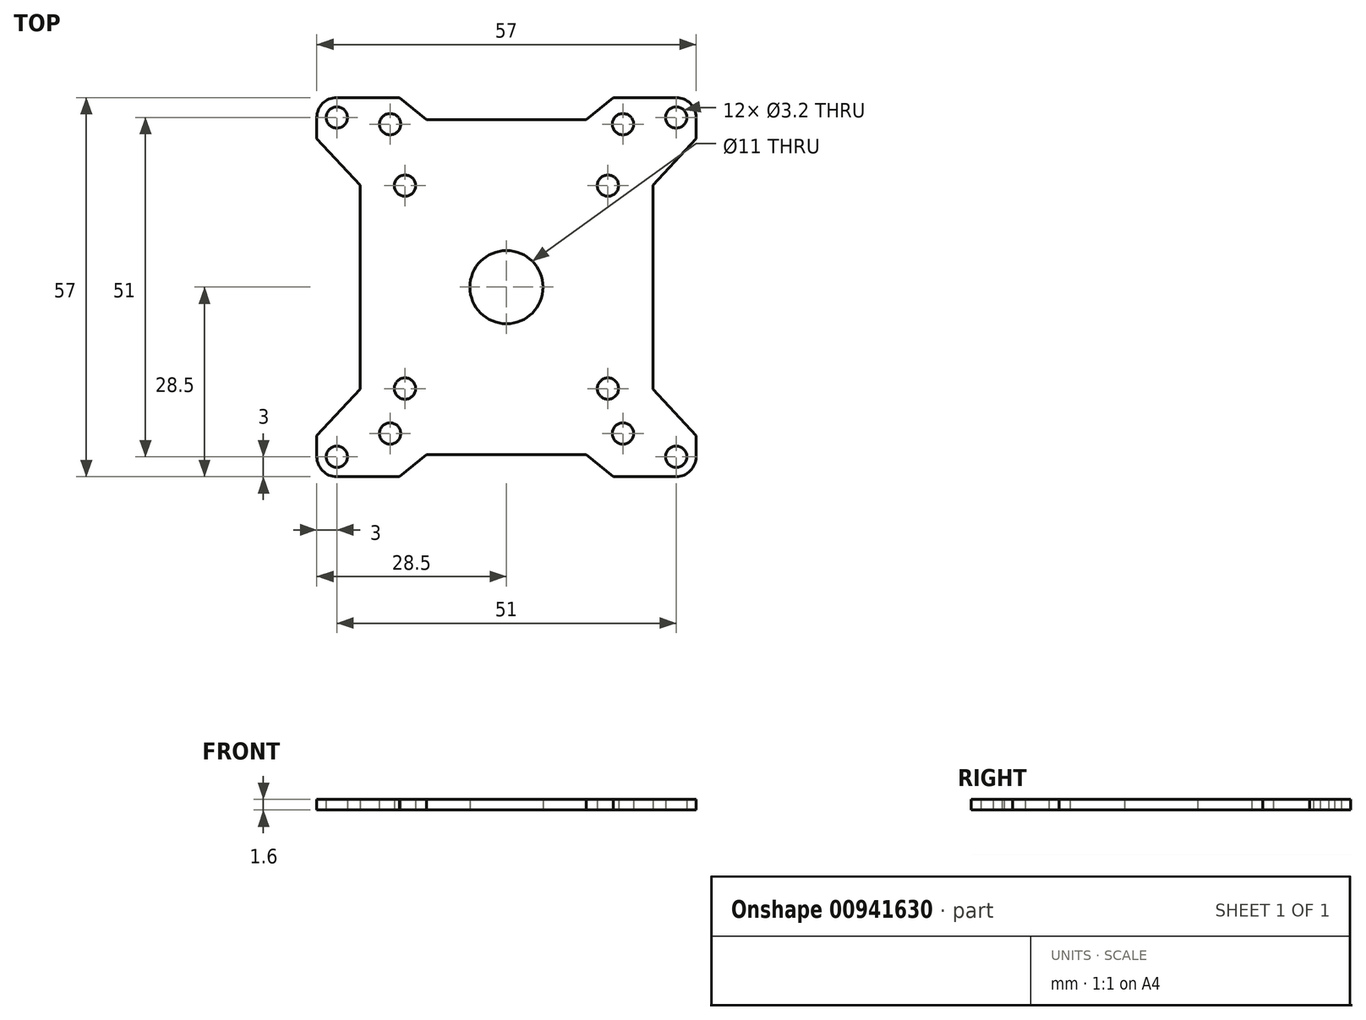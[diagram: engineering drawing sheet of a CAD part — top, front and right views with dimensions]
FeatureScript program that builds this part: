
annotation { "Feature Type Name" : "Feature", "Feature Type Description" : "" }
export const myFeature = defineFeature(function(context is Context, id is Id, definition is map)
    precondition{}
    {
        {
            var Q0;
            Q0=qCreatedBy(makeId("Top.planeOp"),FACE);
            var sketch = newSketch(context, id + "F0", { "sketchPlane" : qUnion([Q0])});
            skCircle(sketch, "E0.0", {"center": v(-17.5, -30) * mm, "radius": 1.6 * mm});
            skCircle(sketch, "E0.1", {"center": v(-17.5, 16.5) * mm, "radius": 1.6 * mm});
            skCircle(sketch, "E0.2", {"center": v(17.5, 16.5) * mm, "radius": 1.6 * mm});
            skCircle(sketch, "E0.3", {"center": v(17.5, -30) * mm, "radius": 1.6 * mm});
            skCircle(sketch, "E0.4", {"center": v(-15.25, 7.25) * mm, "radius": 1.6 * mm});
            skCircle(sketch, "E0.5", {"center": v(-15.25, -23.25) * mm, "radius": 1.6 * mm});
            skCircle(sketch, "E0.6", {"center": v(15.25, 7.25) * mm, "radius": 1.6 * mm});
            skCircle(sketch, "E0.7", {"center": v(15.25, -23.25) * mm, "radius": 1.6 * mm});
            skLineSegment(sketch, "E1", {"start": v(-15.25, 7.25) * mm, "end": v(15.25, -23.25) * mm, "construction": true});
            skLineSegment(sketch, "E2", {"start": v(-15.25, -23.25) * mm, "end": v(15.25, 7.25) * mm, "construction": true});
            skPoint(sketch, "E3", {"position": v(0, -8) * mm});
            skCircle(sketch, "E4.0", {"center": v(25.5, -33.5) * mm, "radius": 1.6 * mm});
            skCircle(sketch, "E4.1", {"center": v(-25.5, -33.5) * mm, "radius": 1.6 * mm});
            skCircle(sketch, "E4.2", {"center": v(-25.5, 17.5) * mm, "radius": 1.6 * mm});
            skPoint(sketch, "E5.visualSharp", {"position": v(-28.5, 20.5) * mm});
            skArc(sketch, "E5.filletArc", {"start": v(-25.5, 20.5) * mm, "mid": v(-27.62, 19.62) * mm, "end": v(-28.5, 17.5) * mm});
            skLineSegment(sketch, "E6", {"start": v(-25.5, 20.5) * mm, "end": v(-16.05, 20.5) * mm});
            skLineSegment(sketch, "E7", {"start": v(-16.05, 20.5) * mm, "end": v(-12, 17.2) * mm});
            skLineSegment(sketch, "E8", {"start": v(-12, 17.2) * mm, "end": v(0, 17.2) * mm});
            skLineSegment(sketch, "E9", {"start": v(-28.5, 17.5) * mm, "end": v(-28.5, 14.32) * mm});
            skLineSegment(sketch, "E10", {"start": v(-28.5, 14.32) * mm, "end": v(-22, 7.31) * mm});
            skLineSegment(sketch, "E11", {"start": v(-22, 7.31) * mm, "end": v(-22, -8) * mm});
            skLineSegment(sketch, "E12", {"start": v(0, -8) * mm, "end": v(-36.69, -8) * mm, "construction": true});
            skLineSegment(sketch, "E13.MirrorCS", {"start": v(-22, -23.31) * mm, "end": v(-22, -8) * mm});
            skLineSegment(sketch, "E14.MirrorCS", {"start": v(-28.5, -30.32) * mm, "end": v(-22, -23.31) * mm});
            skLineSegment(sketch, "E15.MirrorCS", {"start": v(-28.5, -33.5) * mm, "end": v(-28.5, -30.32) * mm});
            skArc(sketch, "E16.MirrorCS", {"start": v(-25.5, -36.5) * mm, "mid": v(-27.62, -35.62) * mm, "end": v(-28.5, -33.5) * mm});
            skLineSegment(sketch, "E17.MirrorCS", {"start": v(-25.5, -36.5) * mm, "end": v(-16.05, -36.5) * mm});
            skLineSegment(sketch, "E18.MirrorCS", {"start": v(-16.05, -36.5) * mm, "end": v(-12, -33.2) * mm});
            skLineSegment(sketch, "E19.MirrorCS", {"start": v(-12, -33.2) * mm, "end": v(0, -33.2) * mm});
            skLineSegment(sketch, "E20.MirrorCS", {"start": v(16.05, -36.5) * mm, "end": v(12, -33.2) * mm});
            skLineSegment(sketch, "E21.MirrorCS", {"start": v(25.5, -36.5) * mm, "end": v(16.05, -36.5) * mm});
            skArc(sketch, "E22.MirrorCS", {"start": v(25.5, -36.5) * mm, "mid": v(27.62, -35.62) * mm, "end": v(28.5, -33.5) * mm});
            skLineSegment(sketch, "E23.MirrorCS", {"start": v(28.5, -33.5) * mm, "end": v(28.5, -30.32) * mm});
            skLineSegment(sketch, "E24.MirrorCS", {"start": v(28.5, -30.32) * mm, "end": v(22, -23.31) * mm});
            skLineSegment(sketch, "E25.MirrorCS", {"start": v(22, -23.31) * mm, "end": v(22, -8) * mm});
            skLineSegment(sketch, "E26.MirrorCS", {"start": v(22, 7.31) * mm, "end": v(22, -8) * mm});
            skLineSegment(sketch, "E27.MirrorCS", {"start": v(28.5, 14.32) * mm, "end": v(22, 7.31) * mm});
            skLineSegment(sketch, "E28.MirrorCS", {"start": v(28.5, 17.5) * mm, "end": v(28.5, 14.32) * mm});
            skArc(sketch, "E29.MirrorCS", {"start": v(25.5, 20.5) * mm, "mid": v(27.62, 19.62) * mm, "end": v(28.5, 17.5) * mm});
            skLineSegment(sketch, "E30.MirrorCS", {"start": v(25.5, 20.5) * mm, "end": v(16.05, 20.5) * mm});
            skLineSegment(sketch, "E31.MirrorCS", {"start": v(16.05, 20.5) * mm, "end": v(12, 17.2) * mm});
            skLineSegment(sketch, "E32.MirrorCS", {"start": v(12, -33.2) * mm, "end": v(0, -33.2) * mm});
            skLineSegment(sketch, "E33.MirrorCS", {"start": v(12, 17.2) * mm, "end": v(0, 17.2) * mm});
            skCircle(sketch, "E34.0", {"center": v(0, -8) * mm, "radius": 5.5 * mm});
            skCircle(sketch, "E35.0", {"center": v(25.5, 17.5) * mm, "radius": 1.6 * mm});
            skSolve(sketch);
        }
        {
            var Q0;
            Q0=qSketchRegion(id+"F0",true);
            extrude(context, id + "F1", {"entities" : qUnion([Q0]), "depth" : 1.6 * mm, "offsetDistance" : 25 * mm});
        }
    });
